# Revit family: VOLCANO_VR_2_AC_01
name_source: partatom
category: Mechanical Equipment
revit_build: Autodesk Revit 2017 (Build: 20170118_1100(x64)
units: mm (PartAtom-declared; Revit-internal decimal feet)

## family parameters
Cut with Voids When Loaded = No
Host = Face
Part Type = Normal
Room Calculation Point = No
Round Connector Dimension = Use Diameter
Shared = No

## types (3) — shared parameters
Connection stub pipe diameter inlet = 19 "
Connection stub pipe diameter outlet = 19 "
Default Elevation = 1219 mm
Device inlet air temperature = 0 °C
Device inlet water temperature = 70 °C
Device outlet water temperature = 50 °C
Electrical Potential = 230 V
Frequency = 50 Hz
Manufacturer = VTS
Motor rated current AC = 1 A
Motor rated rotations [rpm] = 1380
Protection rating = IP 54
Show Range = Yes
URL = http://vtsgroup.pl
Weight = 29.00 kg

## per-type parameters (varying)
| type | AC motor power | Device heating power | Device outlet air temperature | Fan output | Heat exchanger pressure loss | Horizontal range | Medium flow | Model | Vertical range |
| VOLCANO VR 2 HIGH | 280 W | 36 kW | 28 °C | 4850 m³/h | 13.50 Pa | 22000 mm  [stored 72.1785 ft] | 2 m³/h | VR 2 HIGH | 11000 mm  [stored 36.0892 ft] |
| VOLCANO VR 2 MEDIUM | 220 W | 31 kW | 25 °C | 3600 m³/h | 9.80 Pa | 19000 mm | 1 m³/h | VR 2 MEDIUM | 8000 mm  [stored 26.2467 ft] |
| VOLCANO VR 2 LOW | 190 W | 24 kW | 30 °C | 2400 m³/h | 6.20 Pa | 14000 mm  [stored 45.9318 ft] | 1 m³/h | VR 2 LOW | 6000 mm  [stored 19.685 ft] |

note: [stored X ft] marks values corroborated as IEEE doubles in the binary element streams (Revit-internal decimal feet)

## geometry (parser evidence)
native form markers: Sweep x9
no freeform markers — native parametric forms only
